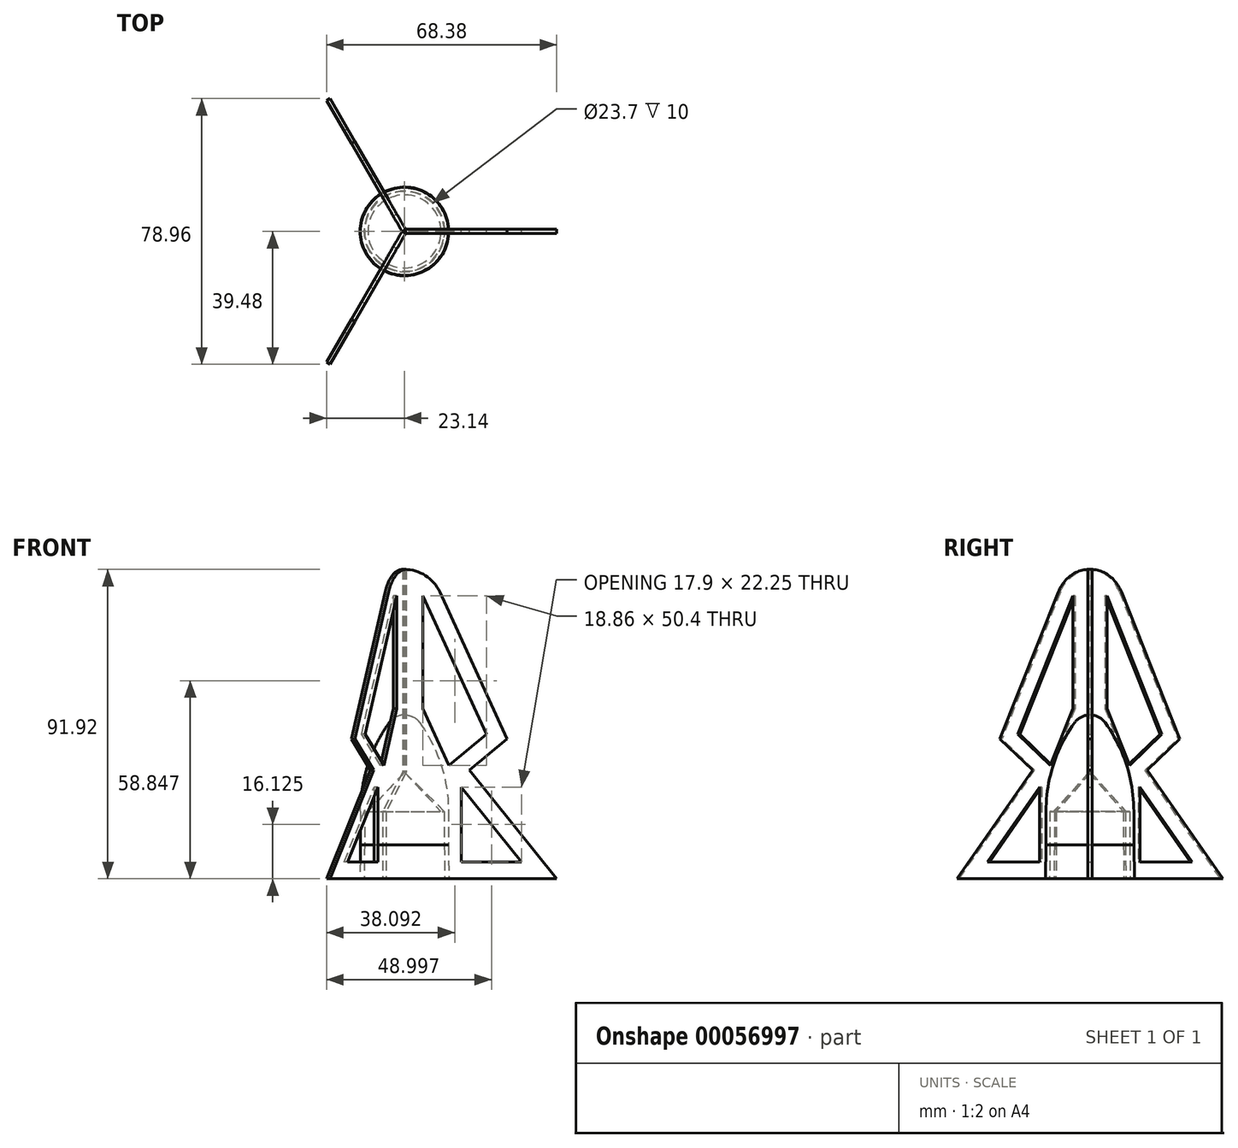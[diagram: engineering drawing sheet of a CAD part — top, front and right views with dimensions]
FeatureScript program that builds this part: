
annotation { "Feature Type Name" : "Feature", "Feature Type Description" : "" }
export const myFeature = defineFeature(function(context is Context, id is Id, definition is map)
    precondition{}
    {
        {
            var Q0;
            Q0=qCreatedBy(makeId("Front.planeOp"),FACE);
            var sketch = newSketch(context, id + "F0", { "sketchPlane" : qUnion([Q0])});
            skLineSegment(sketch, "E0", {"start": v(0, 0) * mm, "end": v(0, 50) * mm, "construction": true});
            skLineSegment(sketch, "E1", {"start": v(0, 0) * mm, "end": v(12, 0) * mm, "construction": true});
            skLineSegment(sketch, "E2", {"start": v(12, 0) * mm, "end": v(11.85, 10) * mm});
            skLineSegment(sketch, "E3", {"start": v(11.85, 10) * mm, "end": v(11.85, 20) * mm});
            skArc(sketch, "E4", {"start": v(11.85, 20) * mm, "mid": v(8.78, 36.13) * mm, "end": v(0, 50) * mm, "construction": true});
            skLineSegment(sketch, "E5", {"start": v(0, 50) * mm, "end": v(0, 31.63) * mm});
            skArc(sketch, "E6.0", {"start": v(13.05, 20) * mm, "mid": v(9.66, 37.15) * mm, "end": v(0, 51.73) * mm});
            skLineSegment(sketch, "E6.1", {"start": v(13.05, 10) * mm, "end": v(13.05, 20) * mm});
            skLineSegment(sketch, "E6.2", {"start": v(13.2, 0.03) * mm, "end": v(13.05, 10) * mm});
            skLineSegment(sketch, "E7", {"start": v(12, 0) * mm, "end": v(13.2, 0.03) * mm});
            skLineSegment(sketch, "E8", {"start": v(0, 50) * mm, "end": v(0, 51.73) * mm});
            skPoint(sketch, "E9.orphan", {"position": v(0, 51.73) * mm});
            skLineSegment(sketch, "E10", {"start": v(11.85, 20) * mm, "end": v(10.85, 20) * mm});
            skLineSegment(sketch, "E11", {"start": v(10.85, 20) * mm, "end": v(0, 31.63) * mm});
            skLineSegment(sketch, "E12", {"start": v(0, 86.72) * mm, "end": v(-0.39, 86.72) * mm, "construction": true});
            skLineSegment(sketch, "E13", {"start": v(0, 50) * mm, "end": v(-2.22, 50) * mm, "construction": true});
            skArc(sketch, "E14", {"start": v(4.56, 46.34) * mm, "mid": v(2.56, 48.06) * mm, "end": v(0, 48.68) * mm});
            skSolve(sketch);
        }
        {
            var Q0;
            Q0=makeQuery(id+"F0.imprint","IMPRINT",FACE,{"disambiguationData":[TD([[makeQuery(id+"F0.imprint","IMPRINT",EDGE,{"derivedFrom":sQuery(id+"F0.wireOp",EDGE,"E2")}),-1.0]])]});
            var Q1;
            Q1=sQuery(id+"F0.wireOp",EDGE,"E0");
            revolve(context, id + "F1", {"entities" : qUnion([Q0]), "axis" : qUnion([Q1]), "revolveType" : RevolveType.FULL});
        }
        {
            var Q0;
            Q0=qCreatedBy(makeId("Front.planeOp"),FACE);
            var sketch = newSketch(context, id + "F2", { "sketchPlane" : qUnion([Q0])});
            skLineSegment(sketch, "E15", {"start": v(13.05, 20) * mm, "end": v(13.05, 10) * mm, "construction": true});
            skLineSegment(sketch, "E16", {"start": v(13.05, 10.01) * mm, "end": v(13.2, 0) * mm, "construction": true});
            skLineSegment(sketch, "E17", {"start": v(-12, 0) * mm, "end": v(-11.85, 10) * mm, "construction": true});
            skLineSegment(sketch, "E18", {"start": v(11.85, 10) * mm, "end": v(12, 0) * mm, "construction": true});
            skLineSegment(sketch, "E19", {"start": v(-11.85, 10) * mm, "end": v(-11.85, 20) * mm, "construction": true});
            skLineSegment(sketch, "E20", {"start": v(11.85, 20) * mm, "end": v(11.85, 10) * mm, "construction": true});
            skLineSegment(sketch, "E21", {"start": v(-10.8, 20.05) * mm, "end": v(0, 31.63) * mm, "construction": true});
            skLineSegment(sketch, "E22", {"start": v(0.05, 31.58) * mm, "end": v(10.8, 20.05) * mm, "construction": true});
            skLineSegment(sketch, "E23", {"start": v(12, 0) * mm, "end": v(45.24, 0) * mm});
            skLineSegment(sketch, "E24", {"start": v(45.24, 0) * mm, "end": v(19.33, 32.21) * mm});
            skLineSegment(sketch, "E25", {"start": v(19.33, 32.21) * mm, "end": v(30.52, 41.6) * mm});
            skLineSegment(sketch, "E26", {"start": v(0, 91.92) * mm, "end": v(0, 31.63) * mm});
            skArc(sketch, "E27", {"start": v(10.5, 85.2) * mm, "mid": v(6.23, 90.1) * mm, "end": v(0, 91.92) * mm});
            skLineSegment(sketch, "E28", {"start": v(10.5, 85.2) * mm, "end": v(30.52, 41.6) * mm});
            skLineSegment(sketch, "E29", {"start": v(0, 31.63) * mm, "end": v(11.85, 20) * mm});
            skLineSegment(sketch, "E30", {"start": v(11.85, 20) * mm, "end": v(11.85, 10) * mm});
            skLineSegment(sketch, "E31", {"start": v(11.85, 10) * mm, "end": v(12, 0) * mm});
            skLineSegment(sketch, "E32", {"start": v(5.52, 84.05) * mm, "end": v(5.52, 50.5) * mm});
            skLineSegment(sketch, "E33", {"start": v(5.52, 50.5) * mm, "end": v(13.26, 33.65) * mm});
            skLineSegment(sketch, "E34", {"start": v(13.26, 33.65) * mm, "end": v(24.38, 42.98) * mm});
            skLineSegment(sketch, "E35", {"start": v(24.38, 42.98) * mm, "end": v(5.52, 84.05) * mm});
            skLineSegment(sketch, "E36", {"start": v(16.9, 27.25) * mm, "end": v(16.9, 5) * mm});
            skLineSegment(sketch, "E37", {"start": v(16.9, 5) * mm, "end": v(34.8, 5) * mm});
            skLineSegment(sketch, "E38", {"start": v(34.8, 5) * mm, "end": v(16.9, 27.25) * mm});
            skSolve(sketch);
        }
        {
            var Q0;
            Q0 = qSketchRegion(id + "F2", true);
            extrude(context, id + "F3", {"entities" : qUnion([Q0]), "endBound" : BoundingType.SYMMETRIC, "depth" : 1.2 * mm});
        }
        {
            var Q0;
            Q0=makeQuery(id+"F3.opExtrude","SWEPT_BODY",BODY,{"disambiguationData":[OSD([sQuery(id+"F2.wireOp",EDGE,"E23"),sQuery(id+"F2.wireOp",EDGE,"E24"),sQuery(id+"F2.wireOp",EDGE,"E25"),sQuery(id+"F2.wireOp",EDGE,"E26"),sQuery(id+"F2.wireOp",EDGE,"E27"),sQuery(id+"F2.wireOp",EDGE,"E28"),sQuery(id+"F2.wireOp",EDGE,"E29"),sQuery(id+"F2.wireOp",EDGE,"E30"),sQuery(id+"F2.wireOp",EDGE,"E31")])]});
            var Q1;
            Q1=sQuery(id+"F0.wireOp",EDGE,"E0");
            circularPattern(context, id + "F4", {"entities" : qUnion([Q0]), "axis" : qUnion([Q1]), "angle" : 360 * degree, "instanceCount" : 3, "equalSpace" : true});
        }
    });
